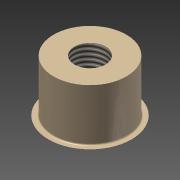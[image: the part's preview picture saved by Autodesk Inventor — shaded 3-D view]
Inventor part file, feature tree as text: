
AUTODESK INVENTOR PART (.ipt)
format: ipt  version: 2015 (Build 190159000, 159)  size: 134,656 bytes
history: native  units: mm
features: sketch x2, other x1, extrude x1, shell x1, revolve x1, fillet x1, thread x1
ambient origin geometry x8: Origin, YZ Plane, XZ Plane, XY Plane, X Axis, Y Axis, Z Axis, Center Point
bodies: Body1 (feature_tree)
feature tree (8):
  other  "Bryła1"
  extrude  "Wyciągnięcie proste1"  Depth=28.0mm
  shell  "Skorupa1"  Thickness=20.0mm
  revolve  "Obrót1"
  fillet  "Zaokrąglenie1"  Radius=8.0mm
  thread  "Gwint1"
  sketch  "Szkic1"
  sketch  "Szkic2"
